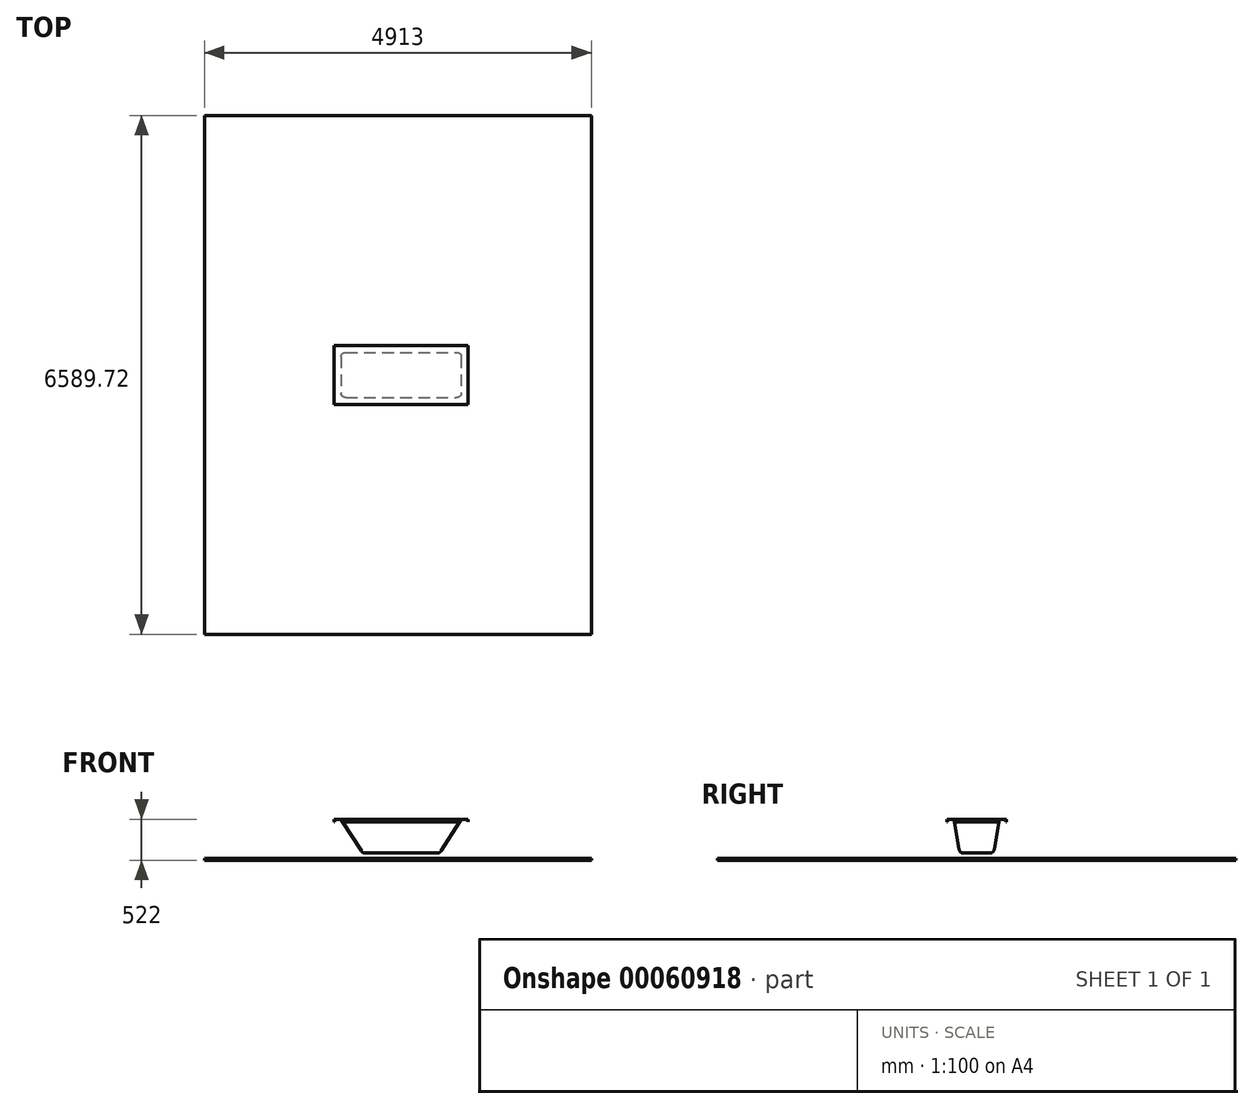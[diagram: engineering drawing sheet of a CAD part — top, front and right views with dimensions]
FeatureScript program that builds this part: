
annotation { "Feature Type Name" : "Feature", "Feature Type Description" : "" }
export const myFeature = defineFeature(function(context is Context, id is Id, definition is map)
    precondition{}
    {
        {
            var Q0;
            Q0=qCreatedBy(makeId("Front.planeOp"),FACE);
            var sketch = newSketch(context, id + "F0", { "sketchPlane" : qUnion([Q0])});
            skLineSegment(sketch, "E0.bottom", {"start": v(-809.08, 152.63) * mm, "end": v(890.92, 152.63) * mm});
            skLineSegment(sketch, "E0.top", {"start": v(-809.08, -277.37) * mm, "end": v(890.92, -277.37) * mm});
            skLineSegment(sketch, "E0.left", {"start": v(-809.08, 152.63) * mm, "end": v(-809.08, -277.37) * mm});
            skLineSegment(sketch, "E0.right", {"start": v(890.92, 152.63) * mm, "end": v(890.92, -277.37) * mm});
            skSolve(sketch);
        }
        {
            var Q0;
            Q0 = qSketchRegion(id + "F0", true);
            extrude(context, id + "F1", {"entities" : qUnion([Q0]), "depth" : 375 * mm, "hasSecondDirection" : true, "secondDirectionOppositeDirection" : true, "secondDirectionDepth" : 375 * mm});
        }
        {
            var Q0;
            Q0=makeQuery(id+"F1.opExtrude","CAP_FACE",FACE,{"disambiguationData":[OSD([sQuery(id+"F0.wireOp",EDGE,"E0.bottom"),sQuery(id+"F0.wireOp",EDGE,"E0.top"),sQuery(id+"F0.wireOp",EDGE,"E0.left"),sQuery(id+"F0.wireOp",EDGE,"E0.right")])],"isStart":false});
            var sketch = newSketch(context, id + "F2", { "sketchPlane" : qUnion([Q0])});
            skLineSegment(sketch, "E1", {"start": v(-809.08, 117.63) * mm, "end": v(-806.08, 117.63) * mm});
            skLineSegment(sketch, "E2", {"start": v(-806.08, 117.63) * mm, "end": v(-806.08, 149.63) * mm});
            skLineSegment(sketch, "E3", {"start": v(-806.08, 149.63) * mm, "end": v(-721.08, 149.63) * mm});
            skLineSegment(sketch, "E4", {"start": v(-721.08, 149.63) * mm, "end": v(-449.08, -277.37) * mm});
            skLineSegment(sketch, "E5", {"start": v(-449.08, -277.37) * mm, "end": v(-809.08, -277.37) * mm});
            skLineSegment(sketch, "E6", {"start": v(-809.08, -277.37) * mm, "end": v(-809.08, 117.63) * mm});
            skLineSegment(sketch, "E7", {"start": v(530.92, -277.37) * mm, "end": v(802.92, 149.63) * mm});
            skLineSegment(sketch, "E8", {"start": v(802.92, 149.63) * mm, "end": v(887.92, 149.63) * mm});
            skLineSegment(sketch, "E9", {"start": v(887.92, 149.63) * mm, "end": v(887.92, 117.63) * mm});
            skLineSegment(sketch, "E10", {"start": v(887.92, 117.63) * mm, "end": v(890.92, 117.63) * mm});
            skLineSegment(sketch, "E11", {"start": v(530.92, -277.37) * mm, "end": v(890.92, -277.37) * mm});
            skLineSegment(sketch, "E12", {"start": v(890.92, -277.37) * mm, "end": v(890.92, 117.63) * mm});
            skSolve(sketch);
        }
        {
            var Q0;
            Q0 = qSketchRegion(id + "F2", true);
            extrude(context, id + "F3", {"entities" : qUnion([Q0]), "operationType" : NewBodyOperationType.REMOVE, "endBound" : BoundingType.THROUGH_ALL, "oppositeDirection" : true, "depth" : 25 * mm});
        }
        {
            var Q0;
            Q0=makeQuery(id+"F1.opExtrude","SWEPT_FACE",FACE,{"disambiguationData":[OSD([sQuery(id+"F0.wireOp",EDGE,"E0.right")])]});
            var sketch = newSketch(context, id + "F4", { "sketchPlane" : qUnion([Q0])});
            skLineSegment(sketch, "E13", {"start": v(-375, 117.63) * mm, "end": v(-372, 117.63) * mm});
            skLineSegment(sketch, "E14", {"start": v(-372, 117.63) * mm, "end": v(-372, 149.63) * mm});
            skLineSegment(sketch, "E15", {"start": v(-372, 149.63) * mm, "end": v(-287, 149.63) * mm});
            skLineSegment(sketch, "E16", {"start": v(-287, 149.63) * mm, "end": v(-215, -277.37) * mm});
            skLineSegment(sketch, "E17", {"start": v(-215, -277.37) * mm, "end": v(-375, -277.37) * mm});
            skLineSegment(sketch, "E18", {"start": v(-375, -277.37) * mm, "end": v(-375, 117.63) * mm});
            skLineSegment(sketch, "E19", {"start": v(375, 117.63) * mm, "end": v(372, 117.63) * mm});
            skLineSegment(sketch, "E20", {"start": v(372, 117.63) * mm, "end": v(372, 149.63) * mm});
            skLineSegment(sketch, "E21", {"start": v(372, 149.63) * mm, "end": v(287, 149.63) * mm});
            skLineSegment(sketch, "E22", {"start": v(287, 149.63) * mm, "end": v(215, -277.37) * mm});
            skLineSegment(sketch, "E23", {"start": v(215, -277.37) * mm, "end": v(375, -277.37) * mm});
            skLineSegment(sketch, "E24", {"start": v(375, -277.37) * mm, "end": v(375, 117.63) * mm});
            skSolve(sketch);
        }
        {
            var Q0;
            Q0 = qSketchRegion(id + "F4", true);
            extrude(context, id + "F5", {"entities" : qUnion([Q0]), "operationType" : NewBodyOperationType.REMOVE, "endBound" : BoundingType.THROUGH_ALL, "oppositeDirection" : true, "depth" : 25 * mm});
        }
        {
            var Q0;
            Q0=makeQuery(id+"F1.opExtrude","SWEPT_FACE",FACE,{"disambiguationData":[OSD([sQuery(id+"F0.wireOp",EDGE,"E0.top")])]});
            var Q1;
            Q1=makeQuery(id+"F5.boolean.opBoolean","INTERSECT",EDGE,{"derivedFrom":[makeQuery(id+"F3.boolean.opBoolean","COPY",FACE,{"derivedFrom":makeQuery(id+"F3.opExtrude","SWEPT_FACE",FACE,{"disambiguationData":[OSD([sQuery(id+"F2.wireOp",EDGE,"E4")])]})}),makeQuery(id+"F5.opExtrude","SWEPT_FACE",FACE,{"disambiguationData":[OSD([sQuery(id+"F4.wireOp",EDGE,"E16")])]})]});
            var Q2;
            Q2=makeQuery(id+"F5.boolean.opBoolean","INTERSECT",EDGE,{"derivedFrom":[makeQuery(id+"F3.boolean.opBoolean","COPY",FACE,{"derivedFrom":makeQuery(id+"F3.opExtrude","SWEPT_FACE",FACE,{"disambiguationData":[OSD([sQuery(id+"F2.wireOp",EDGE,"E4")])]})}),makeQuery(id+"F5.opExtrude","SWEPT_FACE",FACE,{"disambiguationData":[OSD([sQuery(id+"F4.wireOp",EDGE,"E22")])]})]});
            var Q3;
            Q3=makeQuery(id+"F5.boolean.opBoolean","INTERSECT",EDGE,{"derivedFrom":[makeQuery(id+"F3.boolean.opBoolean","COPY",FACE,{"derivedFrom":makeQuery(id+"F3.opExtrude","SWEPT_FACE",FACE,{"disambiguationData":[OSD([sQuery(id+"F2.wireOp",EDGE,"E7")])]})}),makeQuery(id+"F5.opExtrude","SWEPT_FACE",FACE,{"disambiguationData":[OSD([sQuery(id+"F4.wireOp",EDGE,"E16")])]})]});
            var Q4;
            Q4=makeQuery(id+"F5.boolean.opBoolean","INTERSECT",EDGE,{"derivedFrom":[makeQuery(id+"F3.boolean.opBoolean","COPY",FACE,{"derivedFrom":makeQuery(id+"F3.opExtrude","SWEPT_FACE",FACE,{"disambiguationData":[OSD([sQuery(id+"F2.wireOp",EDGE,"E7")])]})}),makeQuery(id+"F5.opExtrude","SWEPT_FACE",FACE,{"disambiguationData":[OSD([sQuery(id+"F4.wireOp",EDGE,"E22")])]})]});
            fillet(context, id + "F6", {"entities" : qUnion([Q0, Q1, Q2, Q3, Q4]), "radius" : 55 * mm, "tangentPropagation" : true, "allowEdgeOverflow" : false});
        }
        {
            var Q0;
            Q0=makeQuery(id+"F1.opExtrude","SWEPT_FACE",FACE,{"disambiguationData":[OSD([sQuery(id+"F0.wireOp",EDGE,"E0.top")])]});
            cPlane(context, id + "F7", {"entities" : qUnion([Q0]), "cplaneType" : CPlaneType.OFFSET, "offset" : 70 * mm, "width" : 150 * mm, "height" : 150 * mm});
        }
        {
            var Q0;
            Q0=qCreatedBy(id+"F7.planeOp",FACE);
            var sketch = newSketch(context, id + "F8", { "sketchPlane" : qUnion([Q0])});
            skLineSegment(sketch, "E25.bottom", {"start": v(2456.5, -3294.86) * mm, "end": v(-2456.5, -3294.86) * mm});
            skLineSegment(sketch, "E25.top", {"start": v(2456.5, 3294.86) * mm, "end": v(-2456.5, 3294.86) * mm});
            skLineSegment(sketch, "E25.left", {"start": v(2456.5, -3294.86) * mm, "end": v(2456.5, 3294.86) * mm});
            skLineSegment(sketch, "E25.right", {"start": v(-2456.5, -3294.86) * mm, "end": v(-2456.5, 3294.86) * mm});
            skPoint(sketch, "E25.middle", {"position": v(0, 0) * mm});
            skSolve(sketch);
        }
        {
            var Q0;
            Q0 = qSketchRegion(id + "F8", true);
            extrude(context, id + "F9", {"entities" : qUnion([Q0]), "depth" : 22 * mm});
        }
    });
